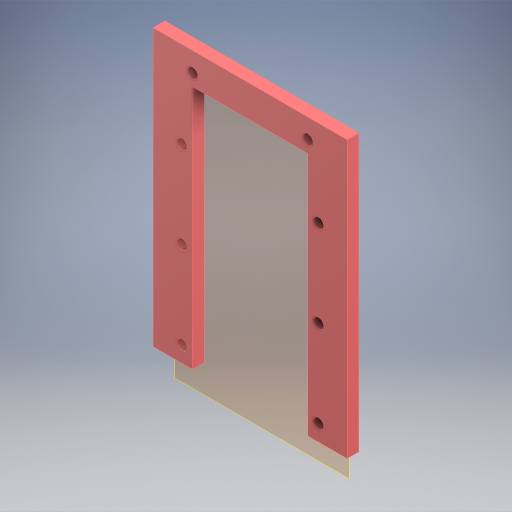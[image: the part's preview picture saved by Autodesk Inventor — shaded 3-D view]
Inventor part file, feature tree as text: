
AUTODESK INVENTOR PART (.ipt)
format: ipt  version: 2024 (Build 280153000, 153)  size: 311,808 bytes
history: native  units: in
note: dims shown in document units (in); Inventor stores cm internally (conversion verified against a paired STEP export)
features: other x4, extrude x1, sketch x1, reference x1
ambient origin geometry x8: Origin, YZ Plane, XZ Plane, XY Plane, X Axis, Y Axis, Z Axis, Center Point
bodies: Body1 (feature_tree)
feature tree (7):
  other  "작업 평면1"
  extrude  "돌출2"  Depth=0.0039in
  sketch  "스케치1"
  reference  "참조1"
  other  "조립품15"
  other  "MX-64T+idle_NEW.ipt:1"
  other  "MX-64T:1"
